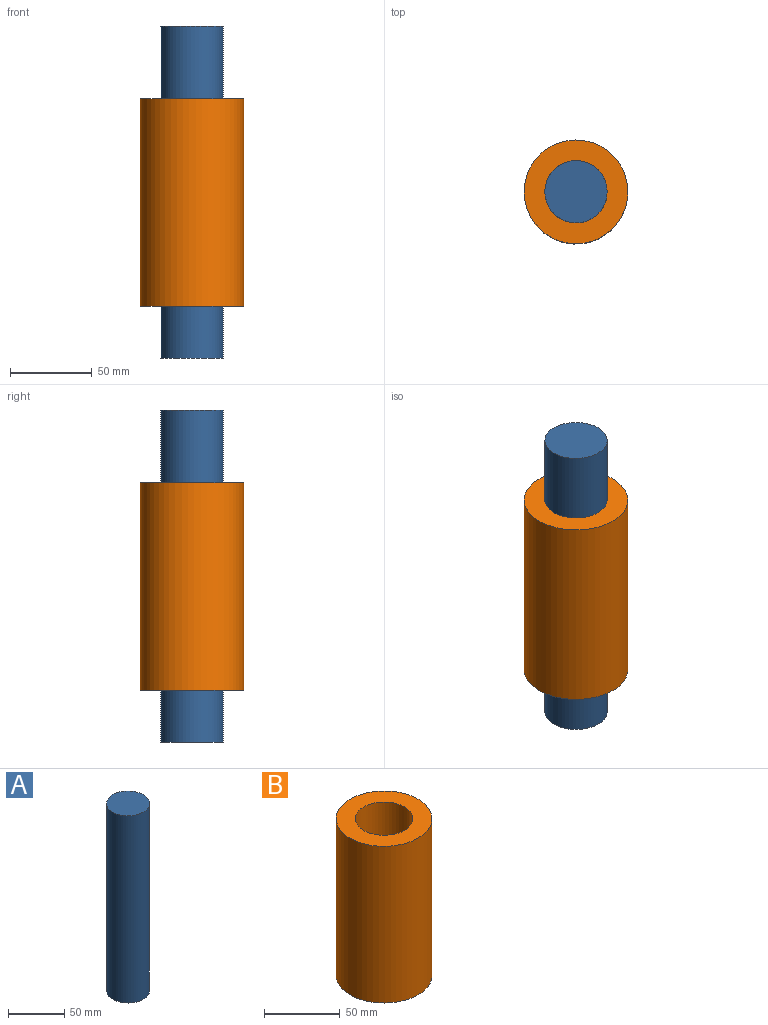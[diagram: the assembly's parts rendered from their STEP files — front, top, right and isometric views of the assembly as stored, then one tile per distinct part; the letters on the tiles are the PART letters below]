
ASSEMBLY  parts=2 mates=1
PART A: 3 faces, bbox 38.1x38.1x203.2 mm
  f0: cylinder r=19.05mm len=203.2mm, axis (0,0,-1), area 24322mm2, adj f1,f2
  f1: plane 38.1x38.1mm, normal (0,0,1), area 1140.1mm2, adj f0
  f2: plane 38.1x38.1mm, normal (0,0,-1), area 1140.1mm2, adj f0
PART B: 4 faces, bbox 63.5x63.5x127 mm
  f0: cylinder r=31.75mm len=127mm, axis (0,0,-1), area 25335.4mm2, adj f1,f2
  f1: plane 63.5x63.5mm, normal (0,0,1), area 2026.8mm2, adj f0,f3
  f2: plane 63.5x63.5mm, normal (0,0,-1), area 2026.8mm2, adj f0,f3
  f3: cylinder r=19.05mm len=127mm, axis (0,0,1), area 15201.2mm2, adj f1,f2
PLACE A t=(-45.74,-26.23,0)mm fixed
PLACE B rot(axis=(0,0,1),133deg) t=(-45.74,-26.23,31.55)mm
MATE cylindrical B.f0 <-> A.f0  axis (0,0,1) through (-45.74,-26.23,158.55)mm
